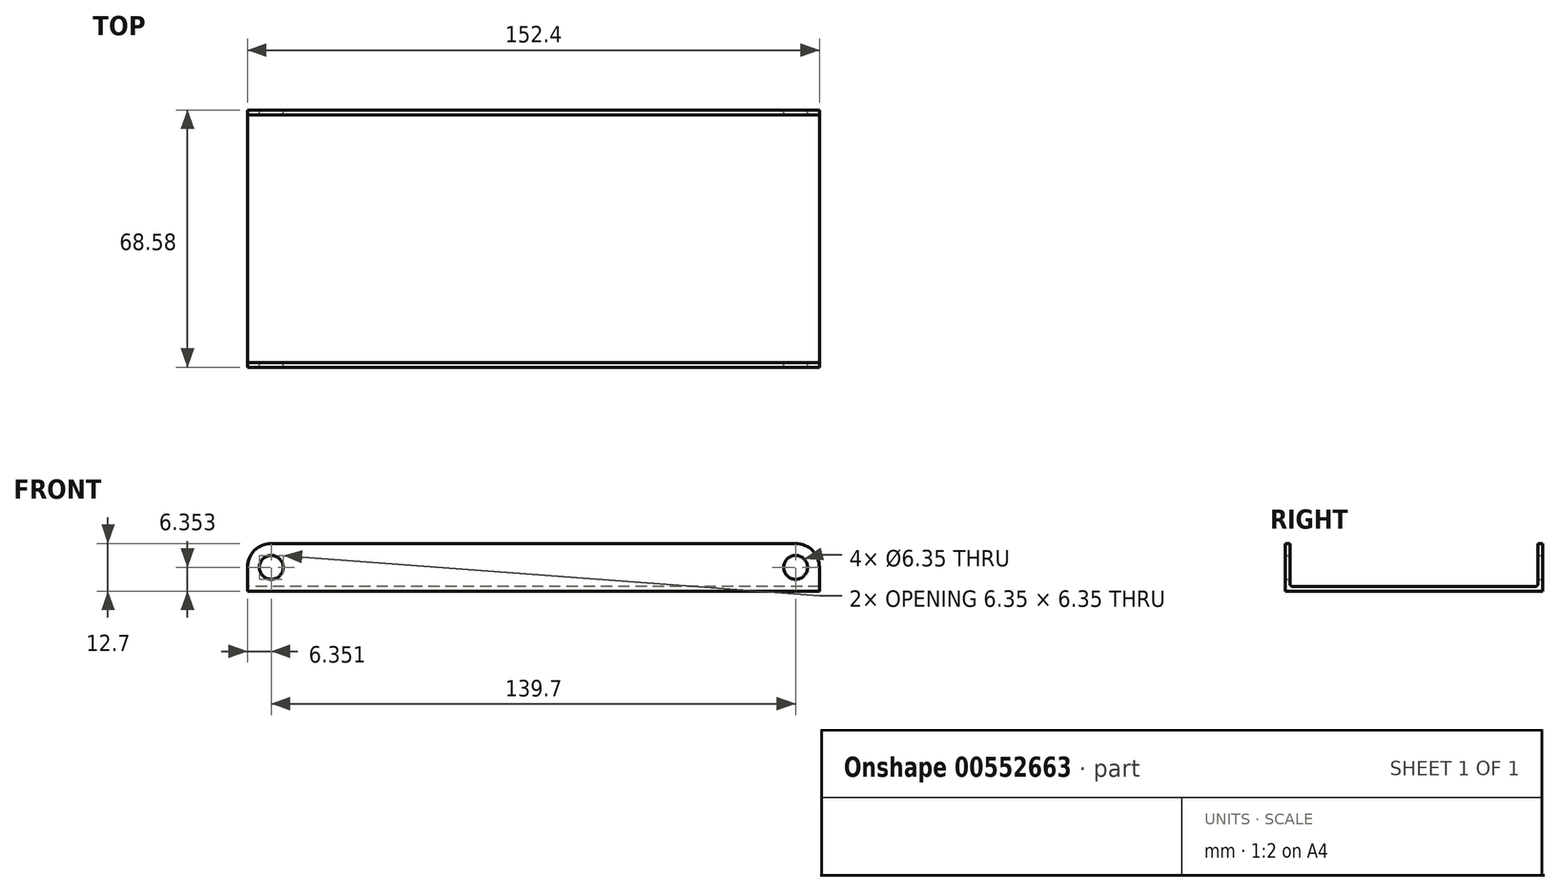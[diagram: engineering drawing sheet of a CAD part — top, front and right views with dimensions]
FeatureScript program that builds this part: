
annotation { "Feature Type Name" : "Feature", "Feature Type Description" : "" }
export const myFeature = defineFeature(function(context is Context, id is Id, definition is map)
    precondition{}
    {
        {
            var Q0;
            Q0=qCreatedBy(makeId("Front.planeOp"),FACE);
            var sketch = newSketch(context, id + "F0", { "sketchPlane" : qUnion([Q0])});
            skLineSegment(sketch, "E0.bottom", {"start": v(-26.44, 11.73) * mm, "end": v(113.26, 11.73) * mm});
            skLineSegment(sketch, "E0.top", {"start": v(-32.79, -0.97) * mm, "end": v(119.61, -0.97) * mm});
            skLineSegment(sketch, "E0.left", {"start": v(-32.79, 5.38) * mm, "end": v(-32.79, -0.97) * mm});
            skLineSegment(sketch, "E0.right", {"start": v(119.61, 5.38) * mm, "end": v(119.61, -0.97) * mm});
            skCircle(sketch, "E1", {"center": v(-26.44, 5.38) * mm, "radius": 3.18 * mm});
            skCircle(sketch, "E2", {"center": v(113.26, 5.38) * mm, "radius": 3.18 * mm});
            skPoint(sketch, "E3.visualSharp", {"position": v(-32.79, 11.73) * mm});
            skArc(sketch, "E3.filletArc", {"start": v(-26.44, 11.73) * mm, "mid": v(-30.93, 9.87) * mm, "end": v(-32.79, 5.38) * mm});
            skPoint(sketch, "E4.visualSharp", {"position": v(119.61, 11.73) * mm});
            skArc(sketch, "E4.filletArc", {"start": v(119.61, 5.38) * mm, "mid": v(117.75, 9.87) * mm, "end": v(113.26, 11.73) * mm});
            skSolve(sketch);
        }
        {
            var Q0;
            Q0 = qSketchRegion(id + "F0", true);
            extrude(context, id + "F1", {"entities" : qUnion([Q0]), "depth" : 68.58 * mm, "offsetDistance" : 25.4 * mm});
        }
        {
            var Q0;
            Q0=makeQuery(id+"F1.opExtrude","SWEPT_FACE",FACE,{"disambiguationData":[OSD([sQuery(id+"F0.wireOp",EDGE,"E0.left")])]});
            cPlane(context, id + "F2", {"entities" : qUnion([Q0]), "cplaneType" : CPlaneType.OFFSET, "offset" : 25.4 * mm, "width" : 152.4 * mm, "height" : 152.4 * mm});
        }
        {
            var Q0;
            Q0=qCreatedBy(id+"F2.planeOp",FACE);
            var sketch = newSketch(context, id + "F3", { "sketchPlane" : qUnion([Q0])});
            skLineSegment(sketch, "E5.bottom", {"start": v(1.27, 25.65) * mm, "end": v(67.31, 25.65) * mm});
            skLineSegment(sketch, "E5.top", {"start": v(1.9, 0.3) * mm, "end": v(66.68, 0.3) * mm});
            skLineSegment(sketch, "E5.left", {"start": v(1.27, 25.65) * mm, "end": v(1.27, 0.94) * mm});
            skLineSegment(sketch, "E5.right", {"start": v(67.31, 25.65) * mm, "end": v(67.31, 0.94) * mm});
            skPoint(sketch, "E6.visualSharp", {"position": v(1.27, 0.3) * mm});
            skArc(sketch, "E6.filletArc", {"start": v(1.27, 0.94) * mm, "mid": v(1.46, 0.49) * mm, "end": v(1.9, 0.3) * mm});
            skPoint(sketch, "E7.visualSharp", {"position": v(67.31, 0.3) * mm});
            skArc(sketch, "E7.filletArc", {"start": v(66.68, 0.3) * mm, "mid": v(67.12, 0.49) * mm, "end": v(67.31, 0.94) * mm});
            skSolve(sketch);
        }
        {
            var Q0;
            Q0 = qSketchRegion(id + "F3", true);
            extrude(context, id + "F4", {"entities" : qUnion([Q0]), "operationType" : NewBodyOperationType.REMOVE, "endBound" : BoundingType.THROUGH_ALL, "oppositeDirection" : true, "depth" : 25.4 * mm, "offsetDistance" : 25.4 * mm});
        }
    });
